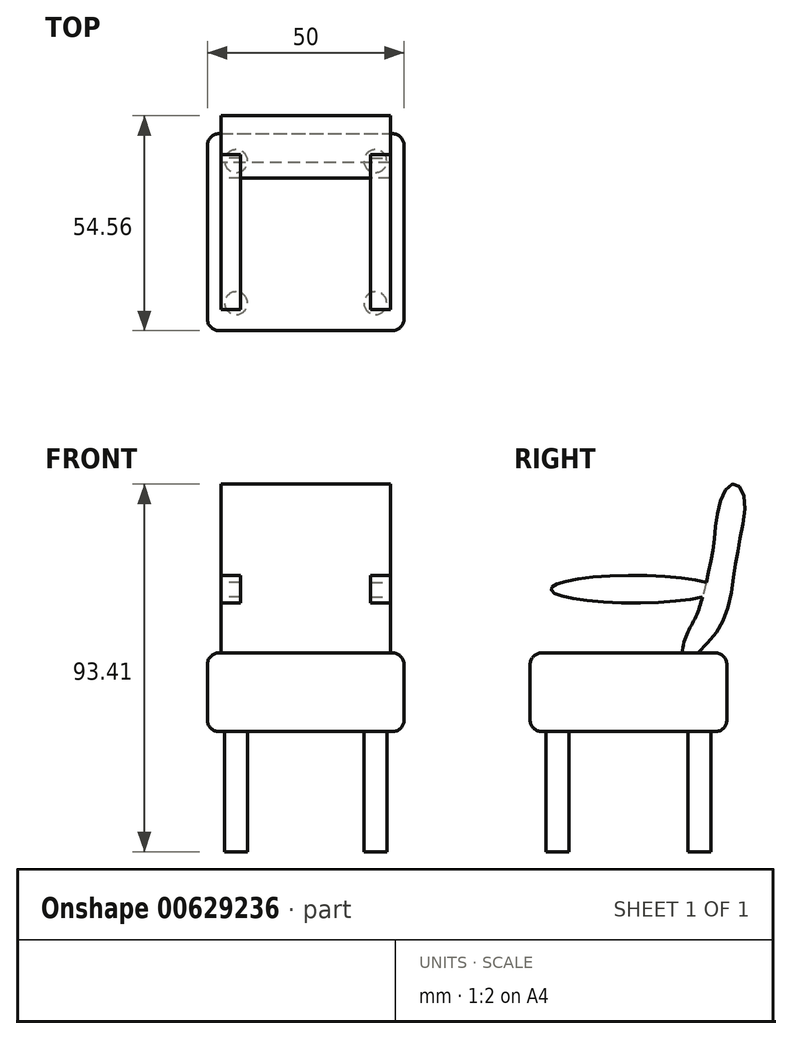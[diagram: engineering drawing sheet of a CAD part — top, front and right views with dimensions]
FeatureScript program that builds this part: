
annotation { "Feature Type Name" : "Feature", "Feature Type Description" : "" }
export const myFeature = defineFeature(function(context is Context, id is Id, definition is map)
    precondition{}
    {
        {
            var Q0;
            Q0=qCreatedBy(makeId("Top.planeOp"),FACE);
            var sketch = newSketch(context, id + "F0", { "sketchPlane" : qUnion([Q0])});
            skLineSegment(sketch, "E0.bottom", {"start": v(-25, -25) * mm, "end": v(25, -25) * mm});
            skLineSegment(sketch, "E0.top", {"start": v(-25, 25) * mm, "end": v(25, 25) * mm});
            skLineSegment(sketch, "E0.left", {"start": v(-25, -25) * mm, "end": v(-25, 25) * mm});
            skLineSegment(sketch, "E0.right", {"start": v(25, -25) * mm, "end": v(25, 25) * mm});
            skPoint(sketch, "E0.middle", {"position": v(0, 0) * mm});
            skSolve(sketch);
        }
        {
            var Q0;
            Q0=makeQuery(id+"F0.imprint","IMPRINT",FACE,{"disambiguationData":[TD([[makeQuery(id+"F0.imprint","IMPRINT",EDGE,{"derivedFrom":sQuery(id+"F0.wireOp",EDGE,"E0.bottom")}),1.0]])]});
            extrude(context, id + "F1", {"entities" : qUnion([Q0]), "depth" : 20 * mm, "offsetDistance" : 25 * mm});
        }
        {
            var Q0;
            Q0=makeQuery(id+"F1.opExtrude","CAP_FACE",FACE,{"disambiguationData":[OSD([sQuery(id+"F0.wireOp",EDGE,"E0.bottom"),sQuery(id+"F0.wireOp",EDGE,"E0.top"),sQuery(id+"F0.wireOp",EDGE,"E0.left"),sQuery(id+"F0.wireOp",EDGE,"E0.right")])],"isStart":false});
            var Q1;
            Q1=makeQuery(id+"F1.opExtrude","SWEPT_FACE",FACE,{"disambiguationData":[OSD([sQuery(id+"F0.wireOp",EDGE,"E0.bottom")])]});
            var Q2;
            Q2=makeQuery(id+"F1.opExtrude","SWEPT_FACE",FACE,{"disambiguationData":[OSD([sQuery(id+"F0.wireOp",EDGE,"E0.right")])]});
            var Q3;
            Q3=makeQuery(id+"F1.opExtrude","CAP_FACE",FACE,{"disambiguationData":[OSD([sQuery(id+"F0.wireOp",EDGE,"E0.bottom"),sQuery(id+"F0.wireOp",EDGE,"E0.top"),sQuery(id+"F0.wireOp",EDGE,"E0.left"),sQuery(id+"F0.wireOp",EDGE,"E0.right")])],"isStart":true});
            var Q4;
            Q4=makeQuery(id+"F1.opExtrude","SWEPT_FACE",FACE,{"disambiguationData":[OSD([sQuery(id+"F0.wireOp",EDGE,"E0.top")])]});
            var Q5;
            Q5=makeQuery(id+"F1.opExtrude","SWEPT_FACE",FACE,{"disambiguationData":[OSD([sQuery(id+"F0.wireOp",EDGE,"E0.left")])]});
            fillet(context, id + "F2", {"entities" : qUnion([Q0, Q1, Q2, Q3, Q4, Q5]), "radius" : 3 * mm, "tangentPropagation" : true, "allowEdgeOverflow" : false});
        }
        {
            var Q0;
            Q0=qCreatedBy(makeId("Right.planeOp"),FACE);
            var sketch = newSketch(context, id + "F3", { "sketchPlane" : qUnion([Q0])});
            skFitSpline(sketch, "E1", {"points": [v(18.96, 21.32) * mm, v(24.59, 29.49) * mm, v(26.95, 41.1) * mm, v(28.58, 50.17) * mm, v(29.12, 60.7) * mm, v(26.4, 62.87) * mm, v(23.14, 57.97) * mm, v(21.86, 49.26) * mm, v(20.78, 42.55) * mm, v(19.32, 36.2) * mm, v(17.15, 29.3) * mm, v(14.24, 23.14) * mm, v(14.24, 18.05) * mm, v(18.96, 21.32) * mm]});
            skSolve(sketch);
        }
        {
            var Q0;
            Q0 = qSketchRegion(id + "F3", true);
            extrude(context, id + "F4", {"entities" : qUnion([Q0]), "operationType" : NewBodyOperationType.ADD, "depth" : 21.5 * mm, "offsetDistance" : 25 * mm});
        }
        {
            var Q0;
            Q0=makeQuery(id+"F1.opExtrude","SWEPT_BODY",BODY,{"disambiguationData":[OSD([sQuery(id+"F0.wireOp",EDGE,"E0.bottom"),sQuery(id+"F0.wireOp",EDGE,"E0.top"),sQuery(id+"F0.wireOp",EDGE,"E0.left"),sQuery(id+"F0.wireOp",EDGE,"E0.right")])]});
            var Q1;
            Q1=qCreatedBy(makeId("Right.planeOp"),FACE);
            mirror(context, id + "F5", {"operationType" : NewBodyOperationType.ADD, "entities" : qUnion([Q0]), "mirrorPlane" : qUnion([Q1])});
        }
        {
            var Q0;
            Q0=makeQuery(id+"F1.opExtrude","CAP_FACE",FACE,{"disambiguationData":[OSD([sQuery(id+"F0.wireOp",EDGE,"E0.bottom"),sQuery(id+"F0.wireOp",EDGE,"E0.top"),sQuery(id+"F0.wireOp",EDGE,"E0.left"),sQuery(id+"F0.wireOp",EDGE,"E0.right")])],"isStart":true});
            var sketch = newSketch(context, id + "F6", { "sketchPlane" : qUnion([Q0])});
            skCircle(sketch, "E2", {"center": v(17.7, 18.05) * mm, "radius": 2.9 * mm});
            skSolve(sketch);
        }
        {
            var Q0;
            Q0=makeQuery(id+"F6.imprint","IMPRINT",FACE,{"disambiguationData":[TD([[makeQuery(id+"F6.imprint","IMPRINT",EDGE,{"derivedFrom":sQuery(id+"F6.wireOp",EDGE,"E2")}),1.0]])]});
            extrude(context, id + "F7", {"entities" : qUnion([Q0]), "depth" : 30.5 * mm, "offsetDistance" : 25 * mm});
        }
        {
            var Q0;
            Q0=makeQuery(id+"F7.opExtrude","SWEPT_BODY",BODY,{"disambiguationData":[OSD([sQuery(id+"F6.wireOp",EDGE,"E2")])]});
            var Q1;
            Q1=qCreatedBy(makeId("Right.planeOp"),FACE);
            mirror(context, id + "F8", {"entities" : qUnion([Q0]), "mirrorPlane" : qUnion([Q1])});
        }
        {
            var Q0;
            Q0=makeQuery(id+"F8.opPattern","COPY",BODY,{"derivedFrom":makeQuery(id+"F7.opExtrude","SWEPT_BODY",BODY,{"disambiguationData":[OSD([sQuery(id+"F6.wireOp",EDGE,"E2")])]}),"instanceName":"1"});
            var Q1;
            Q1=makeQuery(id+"F7.opExtrude","SWEPT_BODY",BODY,{"disambiguationData":[OSD([sQuery(id+"F6.wireOp",EDGE,"E2")])]});
            var Q2;
            Q2=qCreatedBy(makeId("Front.planeOp"),FACE);
            mirror(context, id + "F9", {"operationType" : NewBodyOperationType.ADD, "entities" : qUnion([Q0, Q1]), "mirrorPlane" : qUnion([Q2])});
        }
        {
            var Q0;
            Q0=makeQuery(id+"F4.opExtrude","CAP_FACE",FACE,{"disambiguationData":[OSD([sQuery(id+"F3.wireOp",EDGE,"E1")])],"isStart":false});
            var sketch = newSketch(context, id + "F10", { "sketchPlane" : qUnion([Q0])});
            skEllipse(sketch, "E3", {"center": v(1.36, 36.2) * mm, "majorRadius": 21.05 * mm, "minorRadius": 3.52 * mm, "majorAxis": v(1, 0)});
            skSolve(sketch);
        }
        {
            var Q0;
            {var subQ0=sQuery(id+"F10.wireOp",EDGE,"E3");var subQ1=makeQuery(id+"F4.opExtrude","CAP_EDGE",EDGE,{"disambiguationData":[OSD([sQuery(id+"F3.wireOp",EDGE,"E1")])],"isStart":false});var subQ2=makeQuery(id+"F10.imprint","INTERSECT",VERTEX,{"disambiguationData":[OD(0.0)],"derivedFrom":[subQ1,subQ0]});Q0=makeQuery(id+"F10.imprint","IMPRINT",FACE,{"disambiguationData":[TD([[makeQuery(id+"F10.imprint","IMPRINT",EDGE,{"disambiguationData":[TD([[subQ2,1.0]])],"derivedFrom":subQ0}),1.0]])]});}
            extrude(context, id + "F11", {"entities" : qUnion([Q0]), "oppositeDirection" : true, "depth" : 5 * mm, "offsetDistance" : 25 * mm});
        }
        {
            var Q0;
            Q0=makeQuery(id+"F11.opExtrude","SWEPT_BODY",BODY,{"disambiguationData":[OSD([sQuery(id+"F3.wireOp",EDGE,"E1"),sQuery(id+"F10.wireOp",EDGE,"E3")])]});
            var Q1;
            Q1=qCreatedBy(makeId("Right.planeOp"),FACE);
            mirror(context, id + "F12", {"operationType" : NewBodyOperationType.ADD, "entities" : qUnion([Q0]), "mirrorPlane" : qUnion([Q1])});
        }
    });
